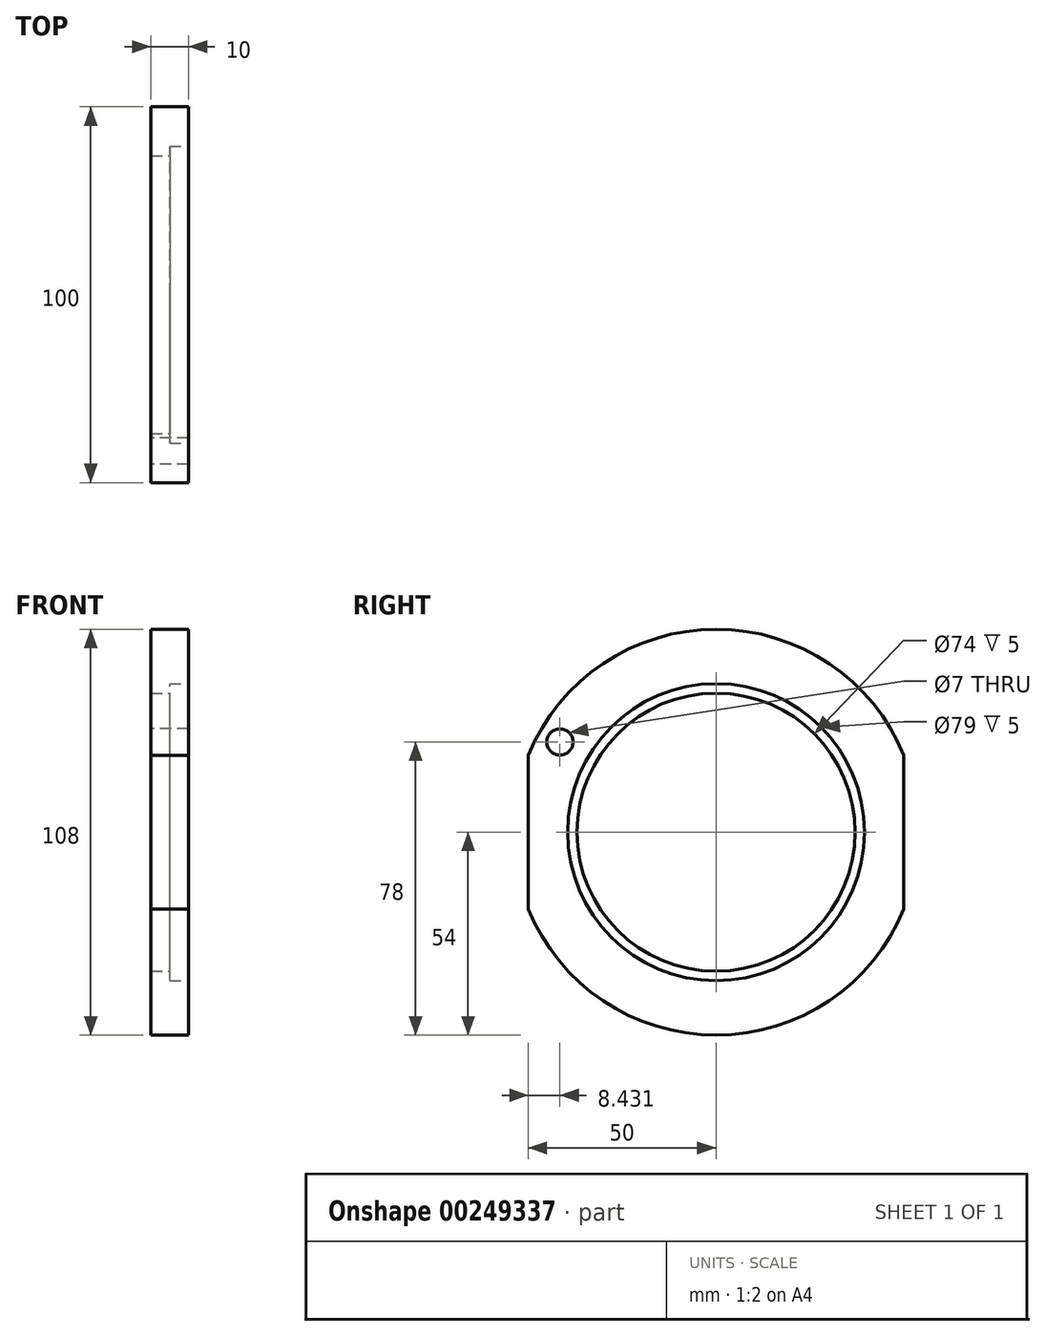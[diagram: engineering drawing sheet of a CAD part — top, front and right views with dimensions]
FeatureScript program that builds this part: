
annotation { "Feature Type Name" : "Feature", "Feature Type Description" : "" }
export const myFeature = defineFeature(function(context is Context, id is Id, definition is map)
    precondition{}
    {
        {
            var Q0;
            Q0=qCreatedBy(makeId("Front.planeOp"),FACE);
            var sketch = newSketch(context, id + "F0", { "sketchPlane" : qUnion([Q0])});
            skLineSegment(sketch, "E0", {"start": v(0, 0) * mm, "end": v(-57.54, 0) * mm, "construction": true});
            skLineSegment(sketch, "E1", {"start": v(0, 54) * mm, "end": v(0, 37) * mm});
            skLineSegment(sketch, "E2", {"start": v(0, 37) * mm, "end": v(10, 37) * mm});
            skLineSegment(sketch, "E3", {"start": v(10, 37) * mm, "end": v(10, 54) * mm});
            skLineSegment(sketch, "E4", {"start": v(0, 54) * mm, "end": v(10, 54) * mm});
            skSolve(sketch);
        }
        {
            var Q0;
            Q0=makeQuery(id+"F0.imprint","IMPRINT",FACE,{"disambiguationData":[TD([[makeQuery(id+"F0.imprint","IMPRINT",EDGE,{"derivedFrom":sQuery(id+"F0.wireOp",EDGE,"E1")}),1.0]])]});
            var Q1;
            Q1=sQuery(id+"F0.wireOp",EDGE,"E0");
            revolve(context, id + "F1", {"entities" : qUnion([Q0]), "axis" : qUnion([Q1]), "revolveType" : RevolveType.FULL});
        }
        {
            var Q0;
            Q0=makeQuery(id+"F1.opRevolve","SWEPT_FACE",FACE,{"disambiguationData":[OSD([sQuery(id+"F0.wireOp",EDGE,"E1")])]});
            var sketch = newSketch(context, id + "F2", { "sketchPlane" : qUnion([Q0])});
            skLineSegment(sketch, "E5", {"start": v(0, 0) * mm, "end": v(41.57, 24) * mm, "construction": true});
            skCircle(sketch, "E6", {"center": v(41.57, 24) * mm, "radius": 3.5 * mm});
            skSolve(sketch);
        }
        {
            var Q0;
            Q0=makeQuery(id+"F2.imprint","IMPRINT",FACE,{"disambiguationData":[TD([[makeQuery(id+"F2.imprint","IMPRINT",EDGE,{"derivedFrom":sQuery(id+"F2.wireOp",EDGE,"E6")}),1.0]])]});
            extrude(context, id + "F3", {"entities" : qUnion([Q0]), "operationType" : NewBodyOperationType.REMOVE, "endBound" : BoundingType.THROUGH_ALL, "oppositeDirection" : true, "depth" : 25 * mm, "offsetDistance" : 25 * mm});
        }
        {
            var Q0;
            Q0=makeQuery(id+"F1.opRevolve","SWEPT_FACE",FACE,{"disambiguationData":[OSD([sQuery(id+"F0.wireOp",EDGE,"E1")])]});
            var sketch = newSketch(context, id + "F4", { "sketchPlane" : qUnion([Q0])});
            skLineSegment(sketch, "E7", {"start": v(-50, 20.4) * mm, "end": v(-50, -20.4) * mm});
            skLineSegment(sketch, "E8", {"start": v(50, -20.4) * mm, "end": v(50, 20.4) * mm});
            skArc(sketch, "E9", {"start": v(50, -20.4) * mm, "mid": v(54, 0) * mm, "end": v(50, 20.4) * mm});
            skArc(sketch, "E10.trimOffspring", {"start": v(-50, 20.4) * mm, "mid": v(-54, 0) * mm, "end": v(-50, -20.4) * mm});
            skSolve(sketch);
        }
        {
            var Q0;
            Q0=makeQuery(id+"F4.imprint","IMPRINT",FACE,{"disambiguationData":[TD([[makeQuery(id+"F4.imprint","IMPRINT",EDGE,{"derivedFrom":sQuery(id+"F4.wireOp",EDGE,"E7")}),-1.0]])]});
            var Q1;
            Q1=makeQuery(id+"F4.imprint","IMPRINT",FACE,{"disambiguationData":[TD([[makeQuery(id+"F4.imprint","IMPRINT",EDGE,{"derivedFrom":sQuery(id+"F4.wireOp",EDGE,"E8")}),-1.0]])]});
            extrude(context, id + "F5", {"entities" : qUnion([Q0, Q1]), "operationType" : NewBodyOperationType.REMOVE, "endBound" : BoundingType.THROUGH_ALL, "oppositeDirection" : true, "depth" : 25 * mm, "offsetDistance" : 25 * mm});
        }
        {
            var Q0;
            Q0=makeQuery(id+"F1.opRevolve","SWEPT_FACE",FACE,{"disambiguationData":[OSD([sQuery(id+"F0.wireOp",EDGE,"E3")])]});
            var sketch = newSketch(context, id + "F6", { "sketchPlane" : qUnion([Q0])});
            skCircle(sketch, "E11", {"center": v(0, 0) * mm, "radius": 39.5 * mm});
            skSolve(sketch);
        }
        {
            var Q0;
            Q0=makeQuery(id+"F6.imprint","IMPRINT",FACE,{"disambiguationData":[TD([[makeQuery(id+"F6.imprint","IMPRINT",EDGE,{"derivedFrom":sQuery(id+"F6.wireOp",EDGE,"E11")}),1.0]])]});
            extrude(context, id + "F7", {"entities" : qUnion([Q0]), "operationType" : NewBodyOperationType.REMOVE, "oppositeDirection" : true, "depth" : 5 * mm, "offsetDistance" : 25 * mm});
        }
    });
